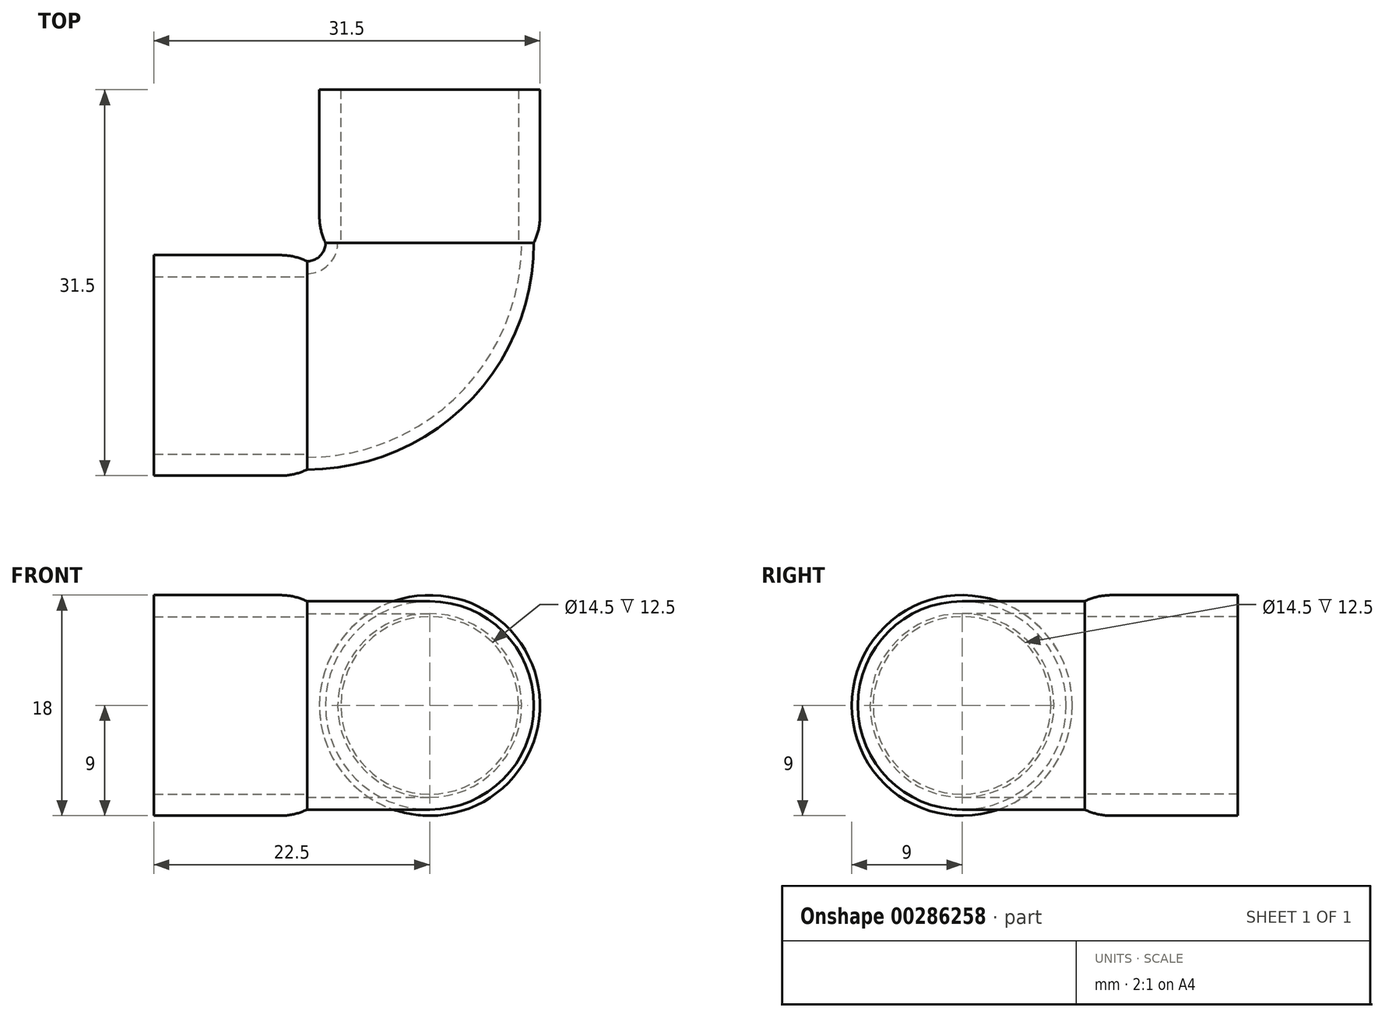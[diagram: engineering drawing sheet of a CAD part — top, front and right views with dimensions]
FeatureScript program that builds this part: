
annotation { "Feature Type Name" : "Feature", "Feature Type Description" : "" }
export const myFeature = defineFeature(function(context is Context, id is Id, definition is map)
    precondition{}
    {
        {
            var Q0;
            Q0=qCreatedBy(makeId("Front.planeOp"),FACE);
            var sketch = newSketch(context, id + "F0", { "sketchPlane" : qUnion([Q0])});
            skCircle(sketch, "E0", {"center": v(0, 0) * mm, "radius": 8.5 * mm});
            skCircle(sketch, "E1", {"center": v(0, 0) * mm, "radius": 7.5 * mm});
            skLineSegment(sketch, "E2", {"start": v(-10, 7.5) * mm, "end": v(-10, -7.15) * mm});
            skSolve(sketch);
        }
        {
            var Q0;
            Q0=makeQuery(id+"F0.imprint","IMPRINT",FACE,{"disambiguationData":[TD([[makeQuery(id+"F0.imprint","IMPRINT",EDGE,{"derivedFrom":sQuery(id+"F0.wireOp",EDGE,"E0")}),1.0]])]});
            var Q1;
            Q1=sQuery(id+"F0.wireOp",EDGE,"E2");
            revolve(context, id + "F1", {"entities" : qUnion([Q0]), "axis" : qUnion([Q1]), "revolveType" : RevolveType.ONE_DIRECTION, "angle" : 90 * degree});
        }
        {
            var Q0;
            Q0=qCreatedBy(makeId("Front.planeOp"),FACE);
            var sketch = newSketch(context, id + "F2", { "sketchPlane" : qUnion([Q0])});
            skCircle(sketch, "E3", {"center": v(0, 0) * mm, "radius": 7.25 * mm});
            skCircle(sketch, "E4", {"center": v(0, 0) * mm, "radius": 9 * mm});
            skSolve(sketch);
        }
        {
            var Q0;
            Q0=makeQuery(id+"F2.imprint","IMPRINT",FACE,{"disambiguationData":[TD([[makeQuery(id+"F2.imprint","IMPRINT",EDGE,{"derivedFrom":sQuery(id+"F2.wireOp",EDGE,"E3")}),-1.0]])]});
            var Q1;
            Q1=sQuery(id+"F2.wireOp",EDGE,"E3");
            var Q2;
            Q2=sQuery(id+"F2.wireOp",EDGE,"E4");
            extrude(context, id + "F3", {"entities" : qUnion([Q0]), "operationType" : NewBodyOperationType.ADD, "surfaceEntities" : qUnion([Q1, Q2]), "oppositeDirection" : true, "depth" : 12.5 * mm});
        }
        {
            var Q0;
            Q0=makeQuery(id+"F1.opRevolve","CAP_FACE",FACE,{"disambiguationData":[OSD([sQuery(id+"F0.wireOp",EDGE,"E0"),sQuery(id+"F0.wireOp",EDGE,"E1")])],"isStart":false});
            var sketch = newSketch(context, id + "F4", { "sketchPlane" : qUnion([Q0])});
            skCircle(sketch, "E5", {"center": v(10, 0) * mm, "radius": 7.25 * mm});
            skCircle(sketch, "E6", {"center": v(10, 0) * mm, "radius": 9 * mm});
            skSolve(sketch);
        }
        {
            var Q0;
            Q0 = qSketchRegion(id + "F4", true);
            extrude(context, id + "F5", {"entities" : qUnion([Q0]), "operationType" : NewBodyOperationType.ADD, "depth" : 12.5 * mm});
        }
        {
            var Q0;
            Q0=makeQuery(id+"F5.opExtrude","CAP_EDGE",EDGE,{"disambiguationData":[OSD([sQuery(id+"F4.wireOp",EDGE,"E6")])],"isStart":true});
            var Q1;
            Q1=makeQuery(id+"F3.opExtrude","CAP_EDGE",EDGE,{"disambiguationData":[OSD([sQuery(id+"F2.wireOp",EDGE,"E4")])],"isStart":true});
            fillet(context, id + "F6", {"entities" : qUnion([Q0, Q1]), "radius" : 5 * mm, "tangentPropagation" : true, "allowEdgeOverflow" : false});
        }
    });
